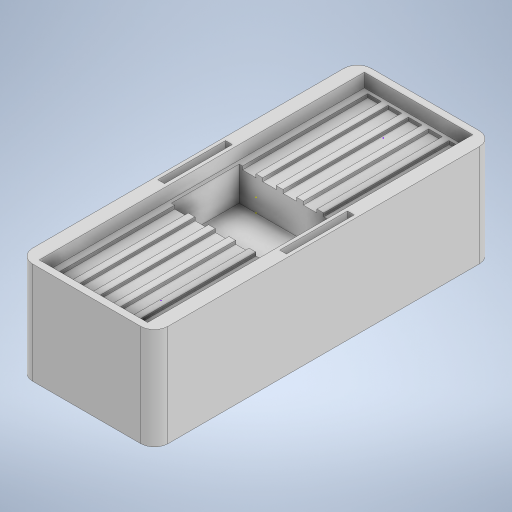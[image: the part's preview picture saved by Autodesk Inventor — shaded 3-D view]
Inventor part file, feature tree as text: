
AUTODESK INVENTOR PART (.ipt)
format: ipt  version: 2023.1 (Build 271208000, 208)  size: 347,136 bytes
history: native  units: mm
features: sketch x8, extrude x5, other x1, fillet x1
ambient origin geometry x8: Origin, YZ Plane, XZ Plane, XY Plane, X Axis, Y Axis, Z Axis, Center Point
bodies: Volumenkörper1 (feature_tree)
feature tree (15):
  extrude  "Extrusion1"  Depth=20.0mm
  extrude  "Extrusion2"  Depth=1.0mm
  sketch  "Skizze4"  dims[d5=1.0mm d6=2.0mm]
  sketch  "Skizze5"  dims[d7=2.0mm d8=2.0mm d9=0.0mm]
  extrude  "Extrusion3"  Depth=2.0mm
  sketch  "Skizze6"  dims[d10=2.0mm d11=0.5mm d12=0.5mm]
  other  "3D-Skizze1"
  sketch  "Skizze8"  dims[d13=0.5mm d14=0.0mm]
  extrude  "Extrusion5"  Depth=2.0mm TaperAngle=0.0deg
  extrude  "Extrusion6"  Depth=0.5mm
  fillet  "Rundung1"  Radius=0.5mm
  sketch  "Skizze1"  dims[d0=50.0mm d1=20.0mm]
  sketch  "Skizze3"  dims[d2=15.0mm d3=0.0mm d4=1.0mm]
  sketch  "Skizze9"  dims[d20=10.0mm]
  sketch  "Skizze10"  dims[d21=25.0mm d23=10.0mm d24=0.5mm d25=1.0mm d26=0.0mm d29=1.0mm d30=0.5mm d31=5.0mm d32=0.0mm d33=2.0mm d34=2.0mm d35=2.0mm d36=2.0mm d37=1.0mm d38=1.0mm d39=1.0mm d40=1.0mm d41=1.0mm d42=1.0mm d43=0.5mm d44=0.5mm d45=10.0mm d46=19.0mm d47=5.0mm d48=0.0mm d49=2.0mm d50=47.0mm d51=0.5mm d52=0.5mm d53=0.5mm d54=0.5mm d55=47.0mm d18=0.5mm d19=0.872665mm]
